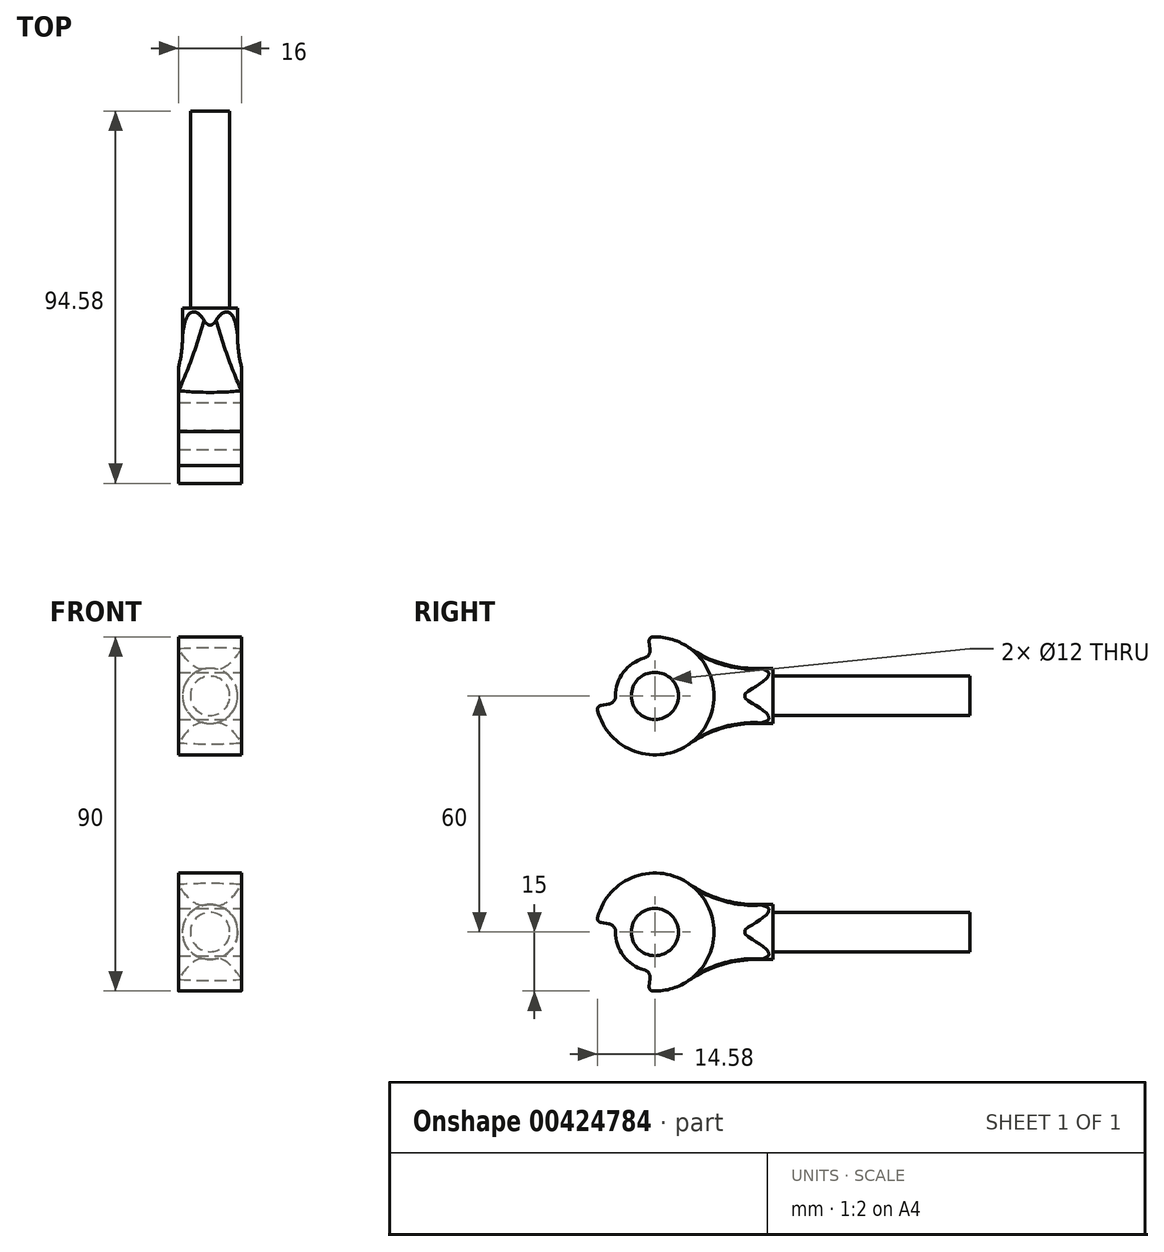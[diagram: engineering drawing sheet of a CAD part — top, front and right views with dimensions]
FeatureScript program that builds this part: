
annotation { "Feature Type Name" : "Feature", "Feature Type Description" : "" }
export const myFeature = defineFeature(function(context is Context, id is Id, definition is map)
    precondition{}
    {
        {
            var Q0;
            Q0=qCreatedBy(makeId("Right.planeOp"),FACE);
            var sketch = newSketch(context, id + "F0", { "sketchPlane" : qUnion([Q0])});
            skArc(sketch, "E0", {"start": v(-0.5, -15) * mm, "mid": v(11.98, 9.03) * mm, "end": v(-14.55, 3.65) * mm});
            skArc(sketch, "E1", {"start": v(-10, 0.07) * mm, "mid": v(-7.99, -6.02) * mm, "end": v(-2.69, -9.63) * mm});
            skLineSegment(sketch, "E2", {"start": v(-1.24, -11.77) * mm, "end": v(-1.46, -13.89) * mm});
            skLineSegment(sketch, "E3", {"start": v(-11.65, 2.05) * mm, "end": v(-13.75, 2.42) * mm});
            skPoint(sketch, "E4.visualSharp", {"position": v(-9.85, 1.74) * mm});
            skArc(sketch, "E4.filletArc", {"start": v(-10, 0.07) * mm, "mid": v(-10.46, 1.37) * mm, "end": v(-11.65, 2.05) * mm});
            skPoint(sketch, "E5.visualSharp", {"position": v(-1.05, -9.95) * mm});
            skArc(sketch, "E5.filletArc", {"start": v(-1.24, -11.77) * mm, "mid": v(-1.57, -10.43) * mm, "end": v(-2.69, -9.63) * mm});
            skPoint(sketch, "E6.visualSharp", {"position": v(-14.77, 2.6) * mm});
            skArc(sketch, "E6.filletArc", {"start": v(-14.55, 3.65) * mm, "mid": v(-14.42, 2.87) * mm, "end": v(-13.75, 2.42) * mm});
            skPoint(sketch, "E7.visualSharp", {"position": v(-1.57, -14.92) * mm});
            skArc(sketch, "E7.filletArc", {"start": v(-1.46, -13.89) * mm, "mid": v(-1.22, -14.65) * mm, "end": v(-0.5, -15) * mm});
            skSolve(sketch);
        }
        {
            var Q0;
            Q0=qSketchRegion(id+"F0",true);
            extrude(context, id + "F1", {"entities" : qUnion([Q0]), "depth" : 8 * mm, "hasSecondDirection" : true, "secondDirectionOppositeDirection" : true, "secondDirectionDepth" : 8 * mm});
        }
        {
            var Q0;
            Q0=qCreatedBy(makeId("Front.planeOp"),FACE);
            var sketch = newSketch(context, id + "F2", { "sketchPlane" : qUnion([Q0])});
            skCircle(sketch, "E8", {"center": v(0, 0) * mm, "radius": 7 * mm});
            skSolve(sketch);
        }
        {
            var Q0;
            Q0=qSketchRegion(id+"F2",true);
            extrude(context, id + "F3", {"entities" : qUnion([Q0]), "operationType" : NewBodyOperationType.ADD, "oppositeDirection" : true, "depth" : 80 * mm});
        }
        {
            var Q0;
            Q0=makeQuery(id+"F3.boolean.opBoolean","INTERSECT",EDGE,{"derivedFrom":[makeQuery(id+"F1.opExtrude","SWEPT_FACE",FACE,{"disambiguationData":[OSD([sQuery(id+"F0.wireOp",EDGE,"E0")])]}),makeQuery(id+"F3.opExtrude","SWEPT_FACE",FACE,{"disambiguationData":[OSD([sQuery(id+"F2.wireOp",EDGE,"E8")])]})]});
            fillet(context, id + "F4", {"entities" : qUnion([Q0]), "radius" : 30 * mm, "tangentPropagation" : true, "allowEdgeOverflow" : false});
        }
        {
            var Q0;
            Q0=makeQuery(id+"F3.opExtrude","CAP_FACE",FACE,{"disambiguationData":[OSD([sQuery(id+"F2.wireOp",EDGE,"E8")])],"isStart":false});
            var sketch = newSketch(context, id + "F5", { "sketchPlane" : qUnion([Q0])});
            skCircle(sketch, "E9", {"center": v(0, 0) * mm, "radius": 5 * mm});
            skCircle(sketch, "E10", {"center": v(0, 0) * mm, "radius": 7 * mm});
            skSolve(sketch);
        }
        {
            var Q0;
            Q0=qSketchRegion(id+"F5",true);
            extrude(context, id + "F6", {"entities" : qUnion([Q0]), "operationType" : NewBodyOperationType.REMOVE, "oppositeDirection" : true, "depth" : 50 * mm});
        }
        {
            var Q0;
            Q0=makeQuery(id+"F1.opExtrude","CAP_FACE",FACE,{"disambiguationData":[OSD([sQuery(id+"F0.wireOp",EDGE,"E0")])],"isStart":false});
            var sketch = newSketch(context, id + "F7", { "sketchPlane" : qUnion([Q0])});
            skCircle(sketch, "E11", {"center": v(0, 0) * mm, "radius": 6 * mm});
            skSolve(sketch);
        }
        {
            var Q0;
            Q0=qSketchRegion(id+"F7",true);
            extrude(context, id + "F8", {"entities" : qUnion([Q0]), "operationType" : NewBodyOperationType.REMOVE, "oppositeDirection" : true, "depth" : 16 * mm});
        }
        {
            var Q0;
            Q0=qCreatedBy(makeId("Top.planeOp"),FACE);
            cPlane(context, id + "F9", {"entities" : qUnion([Q0]), "cplaneType" : CPlaneType.OFFSET, "offset" : 30 * mm, "width" : 150 * mm, "height" : 150 * mm});
        }
        {
            var Q0;
            Q0=makeQuery(id+"F1.opExtrude","SWEPT_BODY",BODY,{"disambiguationData":[OSD([sQuery(id+"F0.wireOp",EDGE,"E0"),sQuery(id+"F0.wireOp",EDGE,"E1"),sQuery(id+"F0.wireOp",EDGE,"E2"),sQuery(id+"F0.wireOp",EDGE,"E3"),sQuery(id+"F0.wireOp",EDGE,"E4.filletArc"),sQuery(id+"F0.wireOp",EDGE,"E5.filletArc"),sQuery(id+"F0.wireOp",EDGE,"E6.filletArc"),sQuery(id+"F0.wireOp",EDGE,"E7.filletArc")])]});
            var Q1;
            Q1=qCreatedBy(id+"F9.planeOp",FACE);
            mirror(context, id + "F10", {"entities" : qUnion([Q0]), "mirrorPlane" : qUnion([Q1])});
        }
    });
